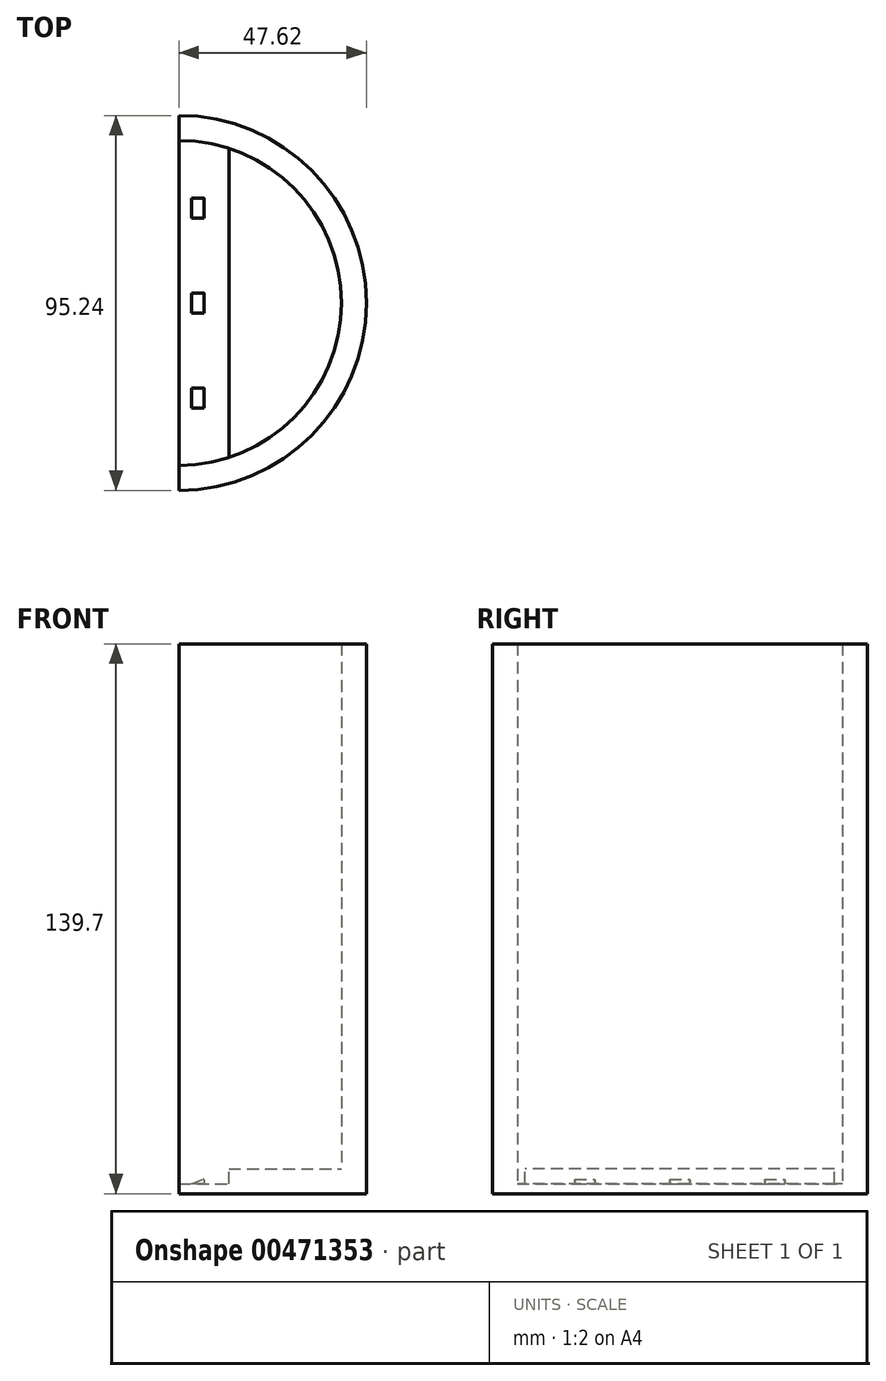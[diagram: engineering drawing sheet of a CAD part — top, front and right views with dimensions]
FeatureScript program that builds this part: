
annotation { "Feature Type Name" : "Feature", "Feature Type Description" : "" }
export const myFeature = defineFeature(function(context is Context, id is Id, definition is map)
    precondition{}
    {
        {
            var Q0;
            Q0=qCreatedBy(makeId("Top.planeOp"),FACE);
            var sketch = newSketch(context, id + "F0", { "sketchPlane" : qUnion([Q0])});
            skArc(sketch, "E0", {"start": v(0, 47.63) * mm, "mid": v(-47.63, 0) * mm, "end": v(0, -47.63) * mm});
            skArc(sketch, "E1", {"start": v(0, 41.28) * mm, "mid": v(-41.28, 0) * mm, "end": v(0, -41.28) * mm});
            skLineSegment(sketch, "E2.bottom", {"start": v(-47.96, 0) * mm, "end": v(-47.95, 0) * mm});
            skLineSegment(sketch, "E2.top", {"start": v(-47.96, -5.19) * mm, "end": v(-47.95, -5.19) * mm});
            skLineSegment(sketch, "E3", {"start": v(0, 47.63) * mm, "end": v(0, 41.28) * mm});
            skLineSegment(sketch, "E4.trimOffspring", {"start": v(0, -41.28) * mm, "end": v(0, -47.63) * mm});
            skSolve(sketch);
        }
        {
            var Q0;
            Q0=qSketchRegion(id+"F0",true);
            extrude(context, id + "F1", {"entities" : qUnion([Q0]), "depth" : 133.35 * mm});
        }
        {
            var Q0;
            Q0=qCreatedBy(makeId("Top.planeOp"),FACE);
            var sketch = newSketch(context, id + "F2", { "sketchPlane" : qUnion([Q0])});
            skArc(sketch, "E5", {"start": v(0, 47.63) * mm, "mid": v(-47.63, 0) * mm, "end": v(0, -47.63) * mm});
            skLineSegment(sketch, "E6", {"start": v(0, -47.63) * mm, "end": v(0, 47.63) * mm});
            skSolve(sketch);
        }
        {
            var Q0;
            Q0=qSketchRegion(id+"F2",true);
            extrude(context, id + "F3", {"entities" : qUnion([Q0]), "operationType" : NewBodyOperationType.ADD, "oppositeDirection" : true, "depth" : 6.35 * mm, "offsetDistance" : 25.4 * mm});
        }
        {
            var Q0;
            Q0=makeQuery(id+"F1.opExtrude","SWEPT_BODY",BODY,{"disambiguationData":[OSD([sQuery(id+"F0.wireOp",EDGE,"E0"),sQuery(id+"F0.wireOp",EDGE,"E1"),sQuery(id+"F0.wireOp",EDGE,"E3"),sQuery(id+"F0.wireOp",EDGE,"E4.trimOffspring")])]});
            var Q1;
            Q1=qCreatedBy(makeId("Right.planeOp"),FACE);
            mirror(context, id + "F4", {"entities" : qUnion([Q0]), "mirrorPlane" : qUnion([Q1])});
        }
        {
            var Q0;
            Q0=makeQuery(id+"F1.opExtrude","SWEPT_BODY",BODY,{"disambiguationData":[OSD([sQuery(id+"F0.wireOp",EDGE,"E0"),sQuery(id+"F0.wireOp",EDGE,"E1"),sQuery(id+"F0.wireOp",EDGE,"E3"),sQuery(id+"F0.wireOp",EDGE,"E4.trimOffspring")])]});
            deleteBodies(context, id + "F5", {"entities" : qUnion([Q0])});
        }
        {
            var Q0;
            Q0=makeQuery(id+"F4.opPattern","COPY",FACE,{"derivedFrom":makeQuery(id+"F3.opExtrude","CAP_FACE",FACE,{"disambiguationData":[OSD([sQuery(id+"F2.wireOp",EDGE,"E5"),sQuery(id+"F2.wireOp",EDGE,"E6")])],"isStart":true}),"instanceName":"1"});
            var sketch = newSketch(context, id + "F6", { "sketchPlane" : qUnion([Q0])});
            skArc(sketch, "E7", {"start": v(0, 41.28) * mm, "mid": v(6.43, 40.77) * mm, "end": v(12.7, 39.27) * mm});
            skLineSegment(sketch, "E8", {"start": v(12.7, 39.27) * mm, "end": v(12.7, -39.27) * mm});
            skLineSegment(sketch, "E9", {"start": v(0, 41.28) * mm, "end": v(0, -41.28) * mm});
            skArc(sketch, "E10.trimOffspring", {"start": v(12.7, -39.27) * mm, "mid": v(6.43, -40.77) * mm, "end": v(0, -41.28) * mm});
            skSolve(sketch);
        }
        {
            var Q0;
            Q0 = qSketchRegion(id + "F6", true);
            extrude(context, id + "F7", {"entities" : qUnion([Q0]), "operationType" : NewBodyOperationType.REMOVE, "oppositeDirection" : true, "depth" : 3.8 * mm, "offsetDistance" : 25.4 * mm});
        }
        {
            var Q0;
            Q0=qCreatedBy(makeId("Front.planeOp"),FACE);
            var sketch = newSketch(context, id + "F8", { "sketchPlane" : qUnion([Q0])});
            skLineSegment(sketch, "E11", {"start": v(6.35, -2.84) * mm, "end": v(6.35, -3.81) * mm});
            skLineSegment(sketch, "E12", {"start": v(6.35, -3.81) * mm, "end": v(3.18, -3.81) * mm});
            skLineSegment(sketch, "E13", {"start": v(3.18, -3.81) * mm, "end": v(6.17, -2.71) * mm});
            skPoint(sketch, "E14.visualSharp", {"position": v(6.35, -2.64) * mm});
            skArc(sketch, "E14.filletArc", {"start": v(6.35, -2.84) * mm, "mid": v(6.3, -2.73) * mm, "end": v(6.17, -2.71) * mm});
            skSolve(sketch);
        }
        {
            var Q0;
            Q0 = qSketchRegion(id + "F8", true);
            extrude(context, id + "F9", {"entities" : qUnion([Q0]), "operationType" : NewBodyOperationType.ADD, "depth" : 2.54 * mm, "offsetDistance" : 25.4 * mm, "hasSecondDirection" : true, "secondDirectionOppositeDirection" : true, "secondDirectionDepth" : 2.54 * mm});
        }
        {
            var Q0;
            Q0=qCreatedBy(makeId("Front.planeOp"),FACE);
            cPlane(context, id + "F10", {"entities" : qUnion([Q0]), "cplaneType" : CPlaneType.OFFSET, "offset" : 24.13 * mm, "width" : 152.4 * mm, "height" : 152.4 * mm});
        }
        {
            var Q0;
            Q0=qCreatedBy(makeId("Front.planeOp"),FACE);
            cPlane(context, id + "F11", {"entities" : qUnion([Q0]), "cplaneType" : CPlaneType.OFFSET, "offset" : 24.13 * mm, "oppositeDirection" : true, "width" : 152.4 * mm, "height" : 152.4 * mm});
        }
        {
            var Q0;
            Q0=qCreatedBy(id+"F10.planeOp",FACE);
            var sketch = newSketch(context, id + "F12", { "sketchPlane" : qUnion([Q0])});
            skLineSegment(sketch, "E15", {"start": v(6.35, -2.83) * mm, "end": v(6.35, -3.8) * mm});
            skLineSegment(sketch, "E16", {"start": v(6.35, -3.8) * mm, "end": v(3.18, -3.8) * mm});
            skLineSegment(sketch, "E17", {"start": v(3.18, -3.8) * mm, "end": v(6.17, -2.7) * mm});
            skPoint(sketch, "E18.visualSharp", {"position": v(6.35, -2.63) * mm});
            skArc(sketch, "E18.filletArc", {"start": v(6.35, -2.83) * mm, "mid": v(6.3, -2.72) * mm, "end": v(6.17, -2.7) * mm});
            skSolve(sketch);
        }
        {
            var Q0;
            Q0 = qSketchRegion(id + "F12", true);
            extrude(context, id + "F13", {"entities" : qUnion([Q0]), "operationType" : NewBodyOperationType.ADD, "depth" : 2.54 * mm, "offsetDistance" : 25.4 * mm, "hasSecondDirection" : true, "secondDirectionOppositeDirection" : true, "secondDirectionDepth" : 2.54 * mm});
        }
        {
            var Q0;
            Q0=qCreatedBy(id+"F11.planeOp",FACE);
            var sketch = newSketch(context, id + "F14", { "sketchPlane" : qUnion([Q0])});
            skLineSegment(sketch, "E19", {"start": v(6.34, -2.83) * mm, "end": v(6.34, -3.8) * mm});
            skLineSegment(sketch, "E20", {"start": v(6.34, -3.8) * mm, "end": v(3.17, -3.8) * mm});
            skLineSegment(sketch, "E21", {"start": v(3.17, -3.8) * mm, "end": v(6.16, -2.7) * mm});
            skPoint(sketch, "E22.visualSharp", {"position": v(6.34, -2.63) * mm});
            skArc(sketch, "E22.filletArc", {"start": v(6.34, -2.83) * mm, "mid": v(6.29, -2.71) * mm, "end": v(6.16, -2.7) * mm});
            skSolve(sketch);
        }
        {
            var Q0;
            Q0 = qSketchRegion(id + "F14", true);
            extrude(context, id + "F15", {"entities" : qUnion([Q0]), "operationType" : NewBodyOperationType.ADD, "depth" : 2.54 * mm, "offsetDistance" : 25.4 * mm, "hasSecondDirection" : true, "secondDirectionOppositeDirection" : true, "secondDirectionDepth" : 2.54 * mm});
        }
        {
            var Q0;
            Q0=makeQuery(id+"F9.opExtrude","SWEPT_EDGE",EDGE,{"disambiguationData":[OSD([sQuery(id+"F8.wireOp",EDGE,"E11"),sQuery(id+"F8.wireOp",EDGE,"E12")])]});
            var Q1;
            Q1=makeQuery(id+"F13.opExtrude","SWEPT_EDGE",EDGE,{"disambiguationData":[OSD([sQuery(id+"F12.wireOp",EDGE,"E15"),sQuery(id+"F12.wireOp",EDGE,"E16")])]});
            var Q2;
            Q2=makeQuery(id+"F15.opExtrude","SWEPT_EDGE",EDGE,{"disambiguationData":[OSD([sQuery(id+"F14.wireOp",EDGE,"E19"),sQuery(id+"F14.wireOp",EDGE,"E20")])]});
            fillet(context, id + "F16", {"entities" : qUnion([Q0, Q1, Q2]), "radius" : 0.13 * mm, "tangentPropagation" : true, "allowEdgeOverflow" : false});
        }
    });
